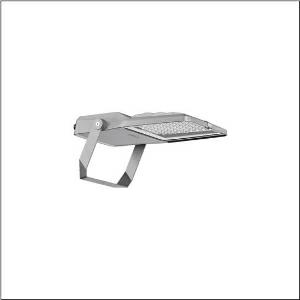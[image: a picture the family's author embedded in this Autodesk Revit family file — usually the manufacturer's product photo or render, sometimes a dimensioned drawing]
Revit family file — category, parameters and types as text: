
# Revit family: floodlight_fl_21_iq_mini___pl33t_5xa7772d4f1a_39e2
name_source: partatom
category: Lighting Fixtures
units: mm (PartAtom-declared; Revit-internal decimal feet)

## family parameters
Cut with Voids When Loaded = No
Host = Face
Light Source = No
Part Type = Normal
Room Calculation Point = No
Round Connector Dimension = Use Diameter
Shared = No

## types (1)
- --- (1 x LED, 18390 lm, 143 W, 4000K)
    Apparent Load = 143 VA
    CIE Flux Codes = 26 75 99 100 100
    Color Rendering = 70
    Color Temperature = 4000K
    Default Elevation = 1800 mm
    Description = Floodlight FL 21 iQ mini, floodlight, primary light control with lens, of PMMA, primary optical cover: protective disc, of toughened safety glass, transparent, light distribution: PL33T, light emission: direct distribution, installation type: surface-mounted, LED, High Power LED, rated luminous flux: 18.390lm, luminous efficacy: 129lm/W, light colour: 740, colour temperature: 4000K, control gear: iQ Street-Remote/DALI, control: Street-Remote, Auto-Match, Temp-Guard, Night-Set, Smart-Wire, Desk-Remote (wireless, voltage-free reading and setting of iQ features in the workshop via application-optimized NFC function/RFID function), optimised constant luminous flux control (CLO 2.0), with terminal, 6-pole, mains connection: 220..240V, AC, 50/60Hz, start of lifetime: 143W, end of service life: 152W, reduction: 61W, luminaire housing, of diecast aluminium, powder-coated, Siteco® metallic grey (DB 702S), corrosivity category C5 mid according to DIN EN ISO 12944, suitable for swimming pools, chlorine-resistant, sealing non-destructively replaceable, mounting bracket, of steel, galvanised, powder-coated, Siteco® metallic grey (DB 702S), protection rating (complete): IP66, insulation class (complete): insulation class II (safety insulation), certification: CE, ENEC, VDE, protection symbol: D, impact resistance: IK08, permissible operating ambient temperature: -40..+40°C, permissible operating ambient temperature for outdoor applications: -40..+50°C, standard: DIN EN 12944, LABS conformity tested according to VDMA 24364:2018-05, packaging unit: 1 piece

Light Distribution: PL33T
    Height = 70 mm
    Lamp = 1 x LED
    Lamp Light Flux = 18390 lm
    Lamp Power = 143 W
    Lamp count = 1
    Length = 485 mm
    Luminous efficacy = 129 lm/W
    Manufacturer = Siteco
    ModVariant = No
    Model = 5XA7772D4F1A
    Number of Poles = 1
    OnlyDefault = Yes
    Power Factor = 1
    Product Name = Floodlight FL 21 iQ mini | PL33T
    Product group = floodlight | pylon annexe
    ProductGroupID = 6200
    Protection Class = Protection class II
    Protection Degree = IP 66
    RLX_Detail_Level = 1
    RLX_Emergency_Light_Flux = 0 lm
    RLX_Emergency_Type = 0
    RLX_Emergency_Type_DB = No
    RlxData = <blob elided: 96497 chars, md5=8a80d4b8>
    Socket = socket
    Standby Power = 0 W
    System Light Flux = 18390 lm
    System Power = 143 W
    Type Comments = factory setting: luminous flux: 100 % | dim-lin: 254 | 730 mA
    Type Image = l_1006845.jpg
    URL = http://relux.com
    VarID = @adj_148856
    Voltage = 0 V
    Weight = 0.00 kg
    Width = 337 mm

## geometry (parser evidence)
native form markers: Blend x4, Sweep x12
no freeform markers — native parametric forms only
